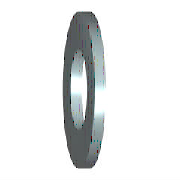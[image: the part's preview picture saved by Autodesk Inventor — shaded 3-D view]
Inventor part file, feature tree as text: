
AUTODESK INVENTOR PART (.ipt)
format: ipt  version: 2015 SP2 (Build 190223200, 223)  size: 105,984 bytes
history: native  units: mm (DEFAULTED — no unit token found)
features: other x1, plane x1, sketch x1
ambient origin geometry x7: Origin, YZ Plane, XY Plane, X Axis, Y Axis, Z Axis, Center Point
bodies: Solid1 (feature_tree), Body (feature_tree)
feature tree (3):
  other  "Work Axis1"
  plane  "Work Plane1"
  sketch  "Sketch"  dims[d0=6.4mm d1=12.0mm d2=1.6mm d3=0.0mm d4=0.0mm d5=0.0mm d6=0.0mm d7=0.0mm]
